# Revit family: CP-primaconsegna
name_source: partatom
category: Modèles génériques
revit_build: Autodesk Revit 2017 (Build: 20160225_1515(x64)
units: mm (PartAtom-declared; Revit-internal decimal feet)

## family parameters
Basée sur le plan de construction = Non
Cote de connecteur circulaire = Utiliser le diamètre
Couper avec des vides une fois chargée = Non
Partagée = Non
Peut héberger une armature = Non
Point de calcul de pièce = Non
Toujours verticalement = Oui
Type d'élément = Normal

## types (5) — shared parameters

## per-type parameters (varying)
| type | C_profondità | larghezza - b |
| variante1-500x500 | 500 mm  [stored 1.64042 ft] | 500 mm  [stored 1.64042 ft] |
| variante2-1500x3000 | 1500 mm  [stored 4.92126 ft] | 1500 mm  [stored 4.92126 ft] |
| variante3-3000x8000 | 3000 mm  [stored 9.84252 ft] | 1500 mm  [stored 4.92126 ft] |
| Type 4 | 6000 mm  [stored 19.685 ft] | 1500 mm  [stored 4.92126 ft] |
| Type 5 | 5000 mm  [stored 16.4042 ft] | 1500 mm  [stored 4.92126 ft] |

note: [stored X ft] marks values corroborated as IEEE doubles in the binary element streams (Revit-internal decimal feet)
